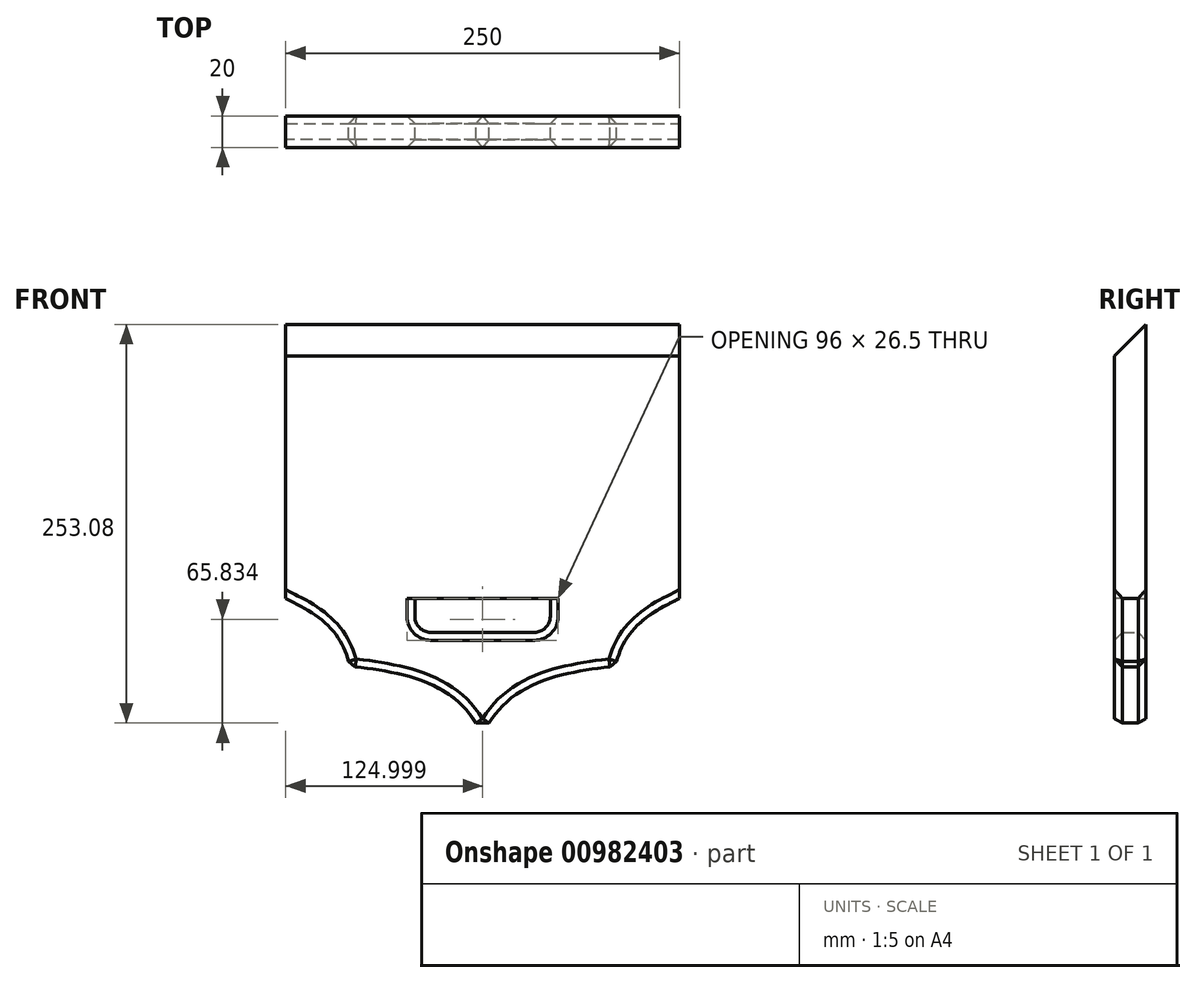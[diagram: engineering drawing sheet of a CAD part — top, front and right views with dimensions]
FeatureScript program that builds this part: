
annotation { "Feature Type Name" : "Feature", "Feature Type Description" : "" }
export const myFeature = defineFeature(function(context is Context, id is Id, definition is map)
    precondition{}
    {
        {
            var Q0;
            Q0=qCreatedBy(makeId("Front.planeOp"),FACE);
            var sketch = newSketch(context, id + "F0", { "sketchPlane" : qUnion([Q0])});
            skLineSegment(sketch, "E0.bottom", {"start": v(128.29, 129.53) * mm, "end": v(-121.71, 129.53) * mm});
            skLineSegment(sketch, "E0.left", {"start": v(128.29, 129.53) * mm, "end": v(128.29, -44.47) * mm});
            skLineSegment(sketch, "E0.right", {"start": v(-121.71, 129.53) * mm, "end": v(-121.71, -44.47) * mm});
            skPoint(sketch, "E0.middle", {"position": v(3.29, 42.53) * mm});
            skPoint(sketch, "E1", {"position": v(-39.71, -44.47) * mm});
            skPoint(sketch, "E2", {"position": v(46.29, -44.47) * mm});
            skLineSegment(sketch, "E3", {"start": v(-39.71, -44.47) * mm, "end": v(46.29, -44.47) * mm});
            skLineSegment(sketch, "E4", {"start": v(36.29, -65.97) * mm, "end": v(-29.71, -65.97) * mm});
            skLineSegment(sketch, "E5", {"start": v(-39.71, -55.97) * mm, "end": v(-39.71, -44.47) * mm});
            skLineSegment(sketch, "E6", {"start": v(46.29, -44.47) * mm, "end": v(46.29, -55.97) * mm});
            skPoint(sketch, "E7.visualSharp", {"position": v(-39.71, -65.97) * mm});
            skArc(sketch, "E7.filletArc", {"start": v(-39.71, -55.97) * mm, "mid": v(-36.78, -63.04) * mm, "end": v(-29.71, -65.97) * mm});
            skPoint(sketch, "E8.visualSharp", {"position": v(46.29, -65.97) * mm});
            skArc(sketch, "E8.filletArc", {"start": v(36.29, -65.97) * mm, "mid": v(43.36, -63.04) * mm, "end": v(46.29, -55.97) * mm});
            skFitSpline(sketch, "E9", {"points": [v(87.29, -87.47) * mm, v(94.03, -71.06) * mm, v(108.17, -55.97) * mm, v(128.29, -44.47) * mm], "startDerivative": vector(17.35, 54.11) * mm, "endDerivative": vector(59.25, 29.55) * mm});
            skFitSpline(sketch, "E10", {"points": [v(3.29, -130.47) * mm, v(15.15, -113.48) * mm, v(35.26, -99.34) * mm, v(61.97, -91.17) * mm, v(87.29, -87.47) * mm], "startDerivative": vector(45.7, 77.12) * mm, "endDerivative": vector(98.22, 11.83) * mm});
            skFitSpline(sketch, "E11.MirrorCS", {"points": [v(3.29, -130.47) * mm, v(-8.57, -113.48) * mm, v(-28.69, -99.34) * mm, v(-55.4, -91.17) * mm, v(-80.71, -87.47) * mm], "startDerivative": vector(-45.7, 77.12) * mm, "endDerivative": vector(-98.22, 11.83) * mm});
            skFitSpline(sketch, "E12.MirrorCS", {"points": [v(-80.71, -87.47) * mm, v(-87.45, -71.06) * mm, v(-101.59, -55.97) * mm, v(-121.71, -44.47) * mm], "startDerivative": vector(-17.35, 54.11) * mm, "endDerivative": vector(-59.25, 29.55) * mm});
            skLineSegment(sketch, "E13.trimOffspring", {"start": v(46.29, -44.47) * mm, "end": v(-39.71, -44.47) * mm});
            skLineSegment(sketch, "E14", {"start": v(3.29, -130.47) * mm, "end": v(164.48, -130.47) * mm, "construction": true});
            skSolve(sketch);
        }
        {
            var Q0;
            Q0 = qSketchRegion(id + "F0", true);
            extrude(context, id + "F1", {"entities" : qUnion([Q0]), "depth" : 20 * mm, "offsetDistance" : 25 * mm});
        }
        {
            var Q0;
            Q0=makeQuery(id+"F1.opExtrude","CAP_EDGE",EDGE,{"disambiguationData":[OSD([sQuery(id+"F0.wireOp",EDGE,"E10")])],"isStart":false});
            var Q1;
            Q1=makeQuery(id+"F1.opExtrude","CAP_EDGE",EDGE,{"disambiguationData":[OSD([sQuery(id+"F0.wireOp",EDGE,"E13.trimOffspring")])],"isStart":false});
            var Q2;
            Q2=makeQuery(id+"F1.opExtrude","CAP_EDGE",EDGE,{"disambiguationData":[OSD([sQuery(id+"F0.wireOp",EDGE,"E4")])],"isStart":false});
            var Q3;
            Q3=makeQuery(id+"F1.opExtrude","CAP_EDGE",EDGE,{"disambiguationData":[OSD([sQuery(id+"F0.wireOp",EDGE,"E7.filletArc")])],"isStart":true});
            var Q4;
            Q4=makeQuery(id+"F1.opExtrude","CAP_EDGE",EDGE,{"disambiguationData":[OSD([sQuery(id+"F0.wireOp",EDGE,"E13.trimOffspring")])],"isStart":true});
            var Q5;
            Q5=makeQuery(id+"F1.opExtrude","CAP_EDGE",EDGE,{"disambiguationData":[OSD([sQuery(id+"F0.wireOp",EDGE,"E9")])],"isStart":false});
            var Q6;
            Q6=makeQuery(id+"F1.opExtrude","CAP_EDGE",EDGE,{"disambiguationData":[OSD([sQuery(id+"F0.wireOp",EDGE,"E11.MirrorCS")])],"isStart":false});
            var Q7;
            Q7=makeQuery(id+"F1.opExtrude","CAP_EDGE",EDGE,{"disambiguationData":[OSD([sQuery(id+"F0.wireOp",EDGE,"E12.MirrorCS")])],"isStart":false});
            var Q8;
            Q8=makeQuery(id+"F1.opExtrude","CAP_EDGE",EDGE,{"disambiguationData":[OSD([sQuery(id+"F0.wireOp",EDGE,"E12.MirrorCS")])],"isStart":true});
            var Q9;
            Q9=makeQuery(id+"F1.opExtrude","CAP_EDGE",EDGE,{"disambiguationData":[OSD([sQuery(id+"F0.wireOp",EDGE,"E11.MirrorCS")])],"isStart":true});
            var Q10;
            Q10=makeQuery(id+"F1.opExtrude","CAP_EDGE",EDGE,{"disambiguationData":[OSD([sQuery(id+"F0.wireOp",EDGE,"E9")])],"isStart":true});
            var Q11;
            Q11=makeQuery(id+"F1.opExtrude","CAP_EDGE",EDGE,{"disambiguationData":[OSD([sQuery(id+"F0.wireOp",EDGE,"E10")])],"isStart":true});
            var Q12;
            Q12=makeQuery(id+"F1.opExtrude","SWEPT_EDGE",EDGE,{"disambiguationData":[OSD([sQuery(id+"F0.wireOp",EDGE,"E10"),sQuery(id+"F0.wireOp",EDGE,"E11.MirrorCS")])]});
            var Q13;
            Q13=makeQuery(id+"F1.opExtrude","SWEPT_EDGE",EDGE,{"disambiguationData":[OSD([sQuery(id+"F0.wireOp",EDGE,"E11.MirrorCS"),sQuery(id+"F0.wireOp",EDGE,"E12.MirrorCS")])]});
            var Q14;
            Q14=makeQuery(id+"F1.opExtrude","SWEPT_EDGE",EDGE,{"disambiguationData":[OSD([sQuery(id+"F0.wireOp",EDGE,"E9"),sQuery(id+"F0.wireOp",EDGE,"E10")])]});
            chamfer(context, id + "F2", {"entities" : qUnion([Q0, Q1, Q2, Q3, Q4, Q5, Q6, Q7, Q8, Q9, Q10, Q11, Q12, Q13, Q14]), "width" : 5 * mm, "tangentPropagation" : true});
        }
        {
            var Q0;
            Q0=makeQuery(id+"F1.opExtrude","CAP_EDGE",EDGE,{"disambiguationData":[OSD([sQuery(id+"F0.wireOp",EDGE,"E0.bottom")])],"isStart":false});
            chamfer(context, id + "F3", {"entities" : qUnion([Q0]), "width" : 20 * mm, "tangentPropagation" : true});
        }
    });
